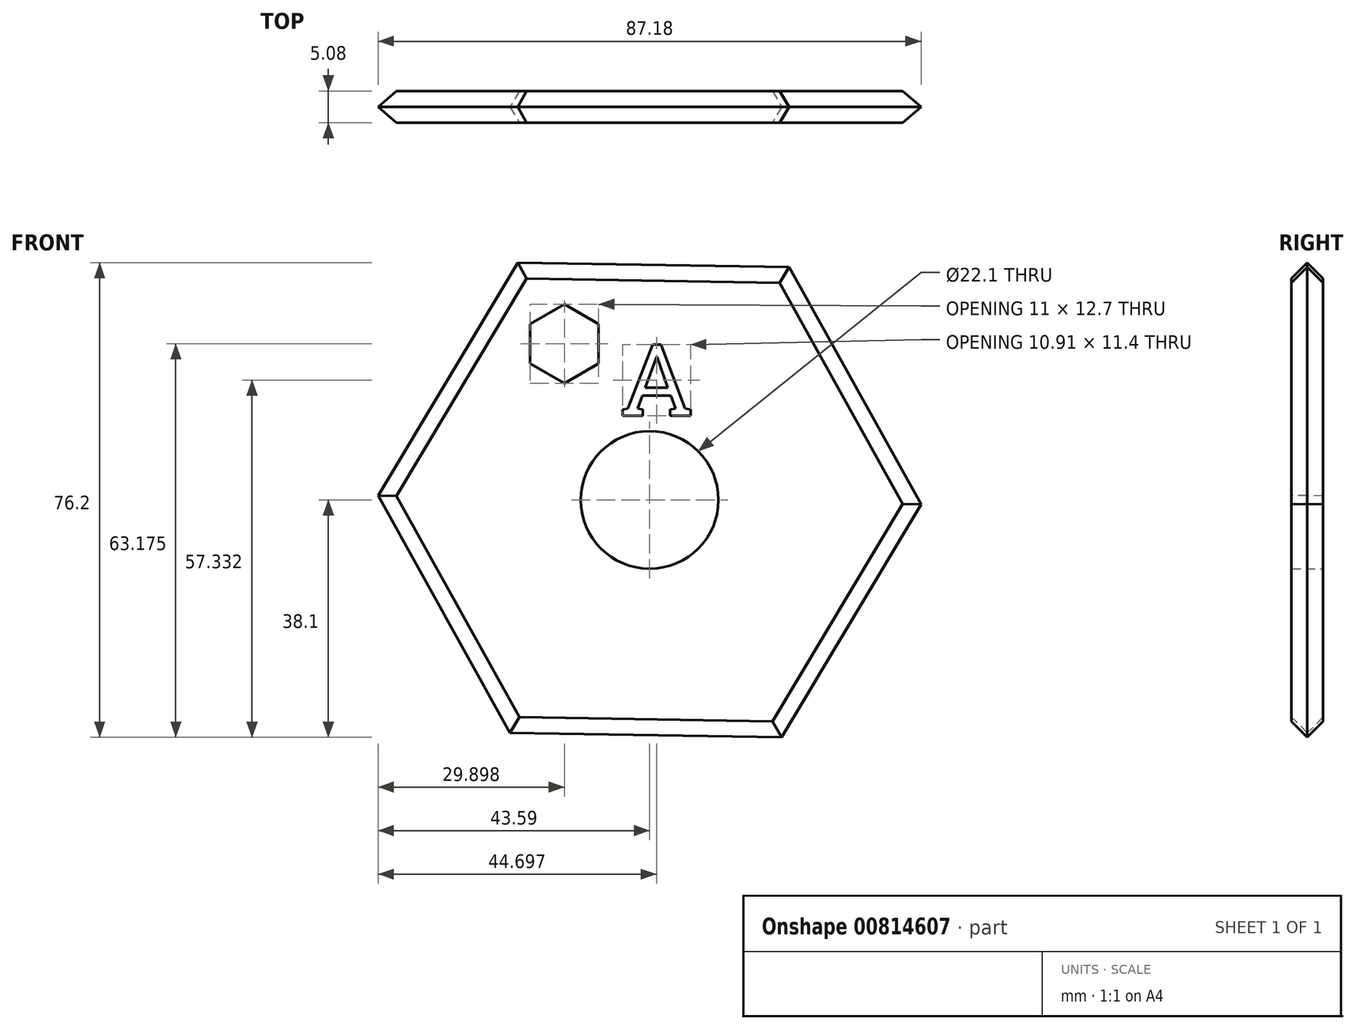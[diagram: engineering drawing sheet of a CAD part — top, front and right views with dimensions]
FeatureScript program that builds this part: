
annotation { "Feature Type Name" : "Feature", "Feature Type Description" : "" }
export const myFeature = defineFeature(function(context is Context, id is Id, definition is map)
    precondition{}
    {
        {
            var Q0;
            Q0=qCreatedBy(makeId("Front.planeOp"),FACE);
            var sketch = newSketch(context, id + "F0", { "sketchPlane" : qUnion([Q0])});
            skCircle(sketch, "E0.cCircle", {"center": v(0, 0) * mm, "radius": 37.75 * mm, "construction": true});
            skLineSegment(sketch, "E0.0", {"start": v(-43.59, 0.7) * mm, "end": v(-21.18, 38.1) * mm});
            skLineSegment(sketch, "E0.1", {"start": v(-21.18, 38.1) * mm, "end": v(22.4, 37.4) * mm});
            skLineSegment(sketch, "E0.2", {"start": v(22.4, 37.4) * mm, "end": v(43.59, -0.7) * mm});
            skLineSegment(sketch, "E0.3", {"start": v(43.59, -0.7) * mm, "end": v(21.18, -38.1) * mm});
            skLineSegment(sketch, "E0.4", {"start": v(21.18, -38.1) * mm, "end": v(-22.4, -37.4) * mm});
            skLineSegment(sketch, "E0.5", {"start": v(-22.4, -37.4) * mm, "end": v(-43.59, 0.7) * mm});
            skPoint(sketch, "E0.0.midPoint", {"position": v(-32.38, 19.4) * mm});
            skCircle(sketch, "E1", {"center": v(0, 0) * mm, "radius": 11.05 * mm});
            skSolve(sketch);
        }
        {
            var Q0;
            Q0=makeQuery(id+"F0.imprint","IMPRINT",FACE,{"disambiguationData":[TD([[makeQuery(id+"F0.imprint","IMPRINT",EDGE,{"derivedFrom":sQuery(id+"F0.wireOp",EDGE,"E0.0")}),-1.0]])]});
            extrude(context, id + "F1", {"entities" : qUnion([Q0]), "depth" : 5.08 * mm, "offsetDistance" : 25.4 * mm});
        }
        {
            var Q0;
            Q0=makeQuery(id+"F1.opExtrude","CAP_FACE",FACE,{"disambiguationData":[OSD([sQuery(id+"F0.wireOp",EDGE,"E0.0"),sQuery(id+"F0.wireOp",EDGE,"E0.1"),sQuery(id+"F0.wireOp",EDGE,"E0.2"),sQuery(id+"F0.wireOp",EDGE,"E0.3"),sQuery(id+"F0.wireOp",EDGE,"E0.4"),sQuery(id+"F0.wireOp",EDGE,"E0.5"),sQuery(id+"F0.wireOp",EDGE,"E1")])],"isStart":false});
            var sketch = newSketch(context, id + "F2", { "sketchPlane" : qUnion([Q0])});
            skCircle(sketch, "E2.cCircle", {"center": v(-13.7, 25.08) * mm, "radius": 5.5 * mm, "construction": true});
            skLineSegment(sketch, "E2.0", {"start": v(-19.2, 21.9) * mm, "end": v(-19.2, 28.25) * mm});
            skLineSegment(sketch, "E2.1", {"start": v(-19.2, 28.25) * mm, "end": v(-13.7, 31.43) * mm});
            skLineSegment(sketch, "E2.2", {"start": v(-13.7, 31.43) * mm, "end": v(-8.2, 28.25) * mm});
            skLineSegment(sketch, "E2.3", {"start": v(-8.2, 28.25) * mm, "end": v(-8.2, 21.9) * mm});
            skLineSegment(sketch, "E2.4", {"start": v(-8.2, 21.9) * mm, "end": v(-13.7, 18.73) * mm});
            skLineSegment(sketch, "E2.5", {"start": v(-13.7, 18.73) * mm, "end": v(-19.2, 21.9) * mm});
            skPoint(sketch, "E2.0.midPoint", {"position": v(-19.2, 25.08) * mm});
            skSolve(sketch);
        }
        {
            var Q0;
            Q0=makeQuery(id+"F2.imprint","IMPRINT",FACE,{"disambiguationData":[TD([[makeQuery(id+"F2.imprint","IMPRINT",EDGE,{"derivedFrom":sQuery(id+"F2.wireOp",EDGE,"E2.0")}),-1.0]])]});
            extrude(context, id + "F3", {"entities" : qUnion([Q0]), "operationType" : NewBodyOperationType.REMOVE, "oppositeDirection" : true, "depth" : 25.4 * mm, "offsetDistance" : 25.4 * mm});
        }
        {
            var Q0;
            Q0=makeQuery(id+"F1.opExtrude","CAP_EDGE",EDGE,{"disambiguationData":[OSD([sQuery(id+"F0.wireOp",EDGE,"E0.1")])],"isStart":false});
            var Q1;
            Q1=makeQuery(id+"F1.opExtrude","CAP_EDGE",EDGE,{"disambiguationData":[OSD([sQuery(id+"F0.wireOp",EDGE,"E0.0")])],"isStart":false});
            var Q2;
            Q2=makeQuery(id+"F1.opExtrude","CAP_EDGE",EDGE,{"disambiguationData":[OSD([sQuery(id+"F0.wireOp",EDGE,"E0.5")])],"isStart":false});
            var Q3;
            Q3=makeQuery(id+"F1.opExtrude","CAP_EDGE",EDGE,{"disambiguationData":[OSD([sQuery(id+"F0.wireOp",EDGE,"E0.4")])],"isStart":false});
            var Q4;
            Q4=makeQuery(id+"F1.opExtrude","CAP_EDGE",EDGE,{"disambiguationData":[OSD([sQuery(id+"F0.wireOp",EDGE,"E0.3")])],"isStart":false});
            var Q5;
            Q5=makeQuery(id+"F1.opExtrude","CAP_EDGE",EDGE,{"disambiguationData":[OSD([sQuery(id+"F0.wireOp",EDGE,"E0.2")])],"isStart":false});
            var Q6;
            Q6=makeQuery(id+"F1.opExtrude","CAP_EDGE",EDGE,{"disambiguationData":[OSD([sQuery(id+"F0.wireOp",EDGE,"E0.1")])],"isStart":true});
            var Q7;
            Q7=makeQuery(id+"F1.opExtrude","CAP_EDGE",EDGE,{"disambiguationData":[OSD([sQuery(id+"F0.wireOp",EDGE,"E0.2")])],"isStart":true});
            var Q8;
            Q8=makeQuery(id+"F1.opExtrude","CAP_EDGE",EDGE,{"disambiguationData":[OSD([sQuery(id+"F0.wireOp",EDGE,"E0.3")])],"isStart":true});
            var Q9;
            Q9=makeQuery(id+"F1.opExtrude","CAP_EDGE",EDGE,{"disambiguationData":[OSD([sQuery(id+"F0.wireOp",EDGE,"E0.4")])],"isStart":true});
            var Q10;
            Q10=makeQuery(id+"F1.opExtrude","CAP_EDGE",EDGE,{"disambiguationData":[OSD([sQuery(id+"F0.wireOp",EDGE,"E0.5")])],"isStart":true});
            var Q11;
            Q11=makeQuery(id+"F1.opExtrude","CAP_EDGE",EDGE,{"disambiguationData":[OSD([sQuery(id+"F0.wireOp",EDGE,"E0.0")])],"isStart":true});
            chamfer(context, id + "F4", {"entities" : qUnion([Q0, Q1, Q2, Q3, Q4, Q5, Q6, Q7, Q8, Q9, Q10, Q11]), "width" : 2.54 * mm, "tangentPropagation" : true});
        }
        {
            var Q0;
            Q0=makeQuery(id+"F1.opExtrude","CAP_FACE",FACE,{"disambiguationData":[OSD([sQuery(id+"F0.wireOp",EDGE,"E0.0"),sQuery(id+"F0.wireOp",EDGE,"E0.1"),sQuery(id+"F0.wireOp",EDGE,"E0.2"),sQuery(id+"F0.wireOp",EDGE,"E0.3"),sQuery(id+"F0.wireOp",EDGE,"E0.4"),sQuery(id+"F0.wireOp",EDGE,"E0.5"),sQuery(id+"F0.wireOp",EDGE,"E1")])],"isStart":false});
            var sketch = newSketch(context, id + "F5", { "sketchPlane" : qUnion([Q0])});
            skText(sketch, "E3", { "text": "A", "fontName": "RobotoSlab-Regular.ttf"});
            skPoint(sketch, "E3.firstSnap0", {"position": v(-19.2, 25.08) * mm});
            const initialGuessF5  = {"E3": [-0.00478, 0.01353, 1, 0, 0.01155]};
            skSetInitialGuess(sketch, initialGuessF5);
            skSolve(sketch);
        }
        {
            var Q0;
            Q0 = qSketchRegion(id + "F5", true);
            extrude(context, id + "F6", {"entities" : qUnion([Q0]), "operationType" : NewBodyOperationType.REMOVE, "oppositeDirection" : true, "depth" : 25.4 * mm, "offsetDistance" : 25.4 * mm});
        }
    });
